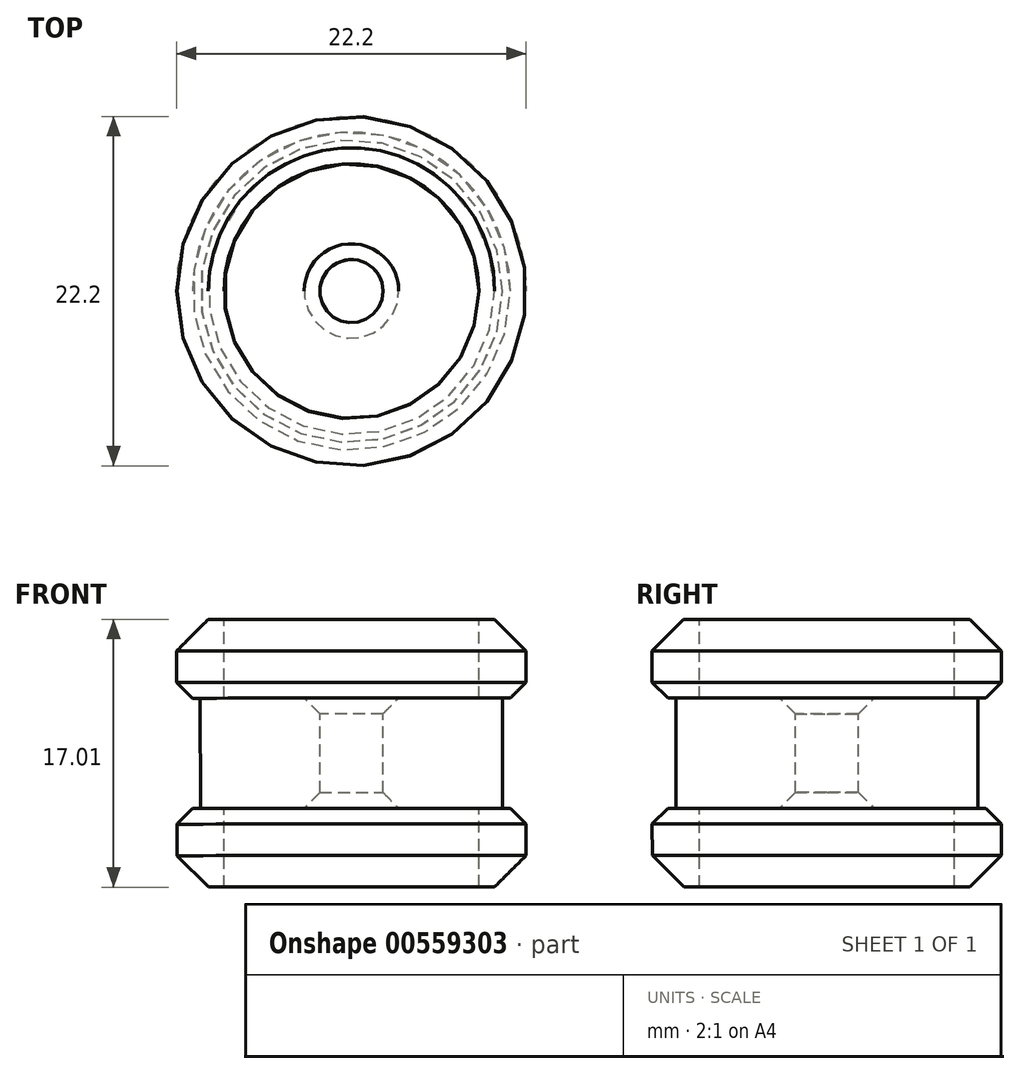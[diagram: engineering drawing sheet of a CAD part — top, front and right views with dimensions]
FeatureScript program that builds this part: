
annotation { "Feature Type Name" : "Feature", "Feature Type Description" : "" }
export const myFeature = defineFeature(function(context is Context, id is Id, definition is map)
    precondition{}
    {
        {
            var Q0;
            Q0=qCreatedBy(makeId("Front.planeOp"),FACE);
            var sketch = newSketch(context, id + "F0", { "sketchPlane" : qUnion([Q0])});
            skLineSegment(sketch, "E0", {"start": v(-8.11, 2.26) * mm, "end": v(8.09, 2.26) * mm, "construction": true});
            skLineSegment(sketch, "E1", {"start": v(8.09, 2.26) * mm, "end": v(11.09, 2.26) * mm});
            skLineSegment(sketch, "E2", {"start": v(11.09, 2.26) * mm, "end": v(11.09, -2.74) * mm});
            skLineSegment(sketch, "E3", {"start": v(11.09, -2.74) * mm, "end": v(8.09, -2.74) * mm});
            skLineSegment(sketch, "E4", {"start": v(8.09, -2.74) * mm, "end": v(8.09, 2.26) * mm});
            skLineSegment(sketch, "E5", {"start": v(9.59, -2.74) * mm, "end": v(9.59, -9.74) * mm});
            skLineSegment(sketch, "E6", {"start": v(8.09, -9.74) * mm, "end": v(11.09, -9.74) * mm});
            skLineSegment(sketch, "E7", {"start": v(11.09, -9.74) * mm, "end": v(11.09, -14.74) * mm});
            skLineSegment(sketch, "E8", {"start": v(11.09, -14.74) * mm, "end": v(8.09, -14.74) * mm});
            skLineSegment(sketch, "E9", {"start": v(8.09, -14.74) * mm, "end": v(8.09, -9.74) * mm});
            skLineSegment(sketch, "E10", {"start": v(-0.01, 2.26) * mm, "end": v(0, -14.74) * mm});
            skLineSegment(sketch, "E11", {"start": v(2, -2.74) * mm, "end": v(0, -2.74) * mm});
            skLineSegment(sketch, "E12", {"start": v(2, -2.74) * mm, "end": v(8.09, -2.74) * mm});
            skLineSegment(sketch, "E13", {"start": v(2, -2.74) * mm, "end": v(2, -9.74) * mm});
            skLineSegment(sketch, "E14", {"start": v(2, -9.74) * mm, "end": v(8.09, -9.74) * mm});
            skSolve(sketch);
        }
        {
            var Q0;
            Q0 = qSketchRegion(id + "F0", true);
            var Q1;
            Q1=sQuery(id+"F0.wireOp",EDGE,"E10");
            revolve(context, id + "F1", {"surfaceOperationType" : NewSurfaceOperationType.NEW, "entities" : qUnion([Q0]), "axis" : qUnion([Q1]), "revolveType" : RevolveType.FULL});
        }
        {
            var Q0;
            Q0=makeQuery(id+"F1.opRevolve","SWEPT_EDGE",EDGE,{"disambiguationData":[OSD([sQuery(id+"F0.wireOp",EDGE,"E7"),sQuery(id+"F0.wireOp",EDGE,"E8")])]});
            var Q1;
            Q1=makeQuery(id+"F1.opRevolve","SWEPT_EDGE",EDGE,{"disambiguationData":[OSD([sQuery(id+"F0.wireOp",EDGE,"E1"),sQuery(id+"F0.wireOp",EDGE,"E2")])]});
            chamfer(context, id + "F2", {"entities" : qUnion([Q0, Q1]), "width" : 2 * mm, "tangentPropagation" : true});
        }
        {
            var Q0;
            Q0=makeQuery(id+"F1.opRevolve","SWEPT_EDGE",EDGE,{"disambiguationData":[OSD([sQuery(id+"F0.wireOp",EDGE,"E2"),sQuery(id+"F0.wireOp",EDGE,"E3")])]});
            var Q1;
            Q1=makeQuery(id+"F1.opRevolve","SWEPT_EDGE",EDGE,{"disambiguationData":[OSD([sQuery(id+"F0.wireOp",EDGE,"E6"),sQuery(id+"F0.wireOp",EDGE,"E7")])]});
            var Q2;
            Q2=makeQuery(id+"F1.opRevolve","SWEPT_EDGE",EDGE,{"disambiguationData":[OSD([sQuery(id+"F0.wireOp",EDGE,"E12"),sQuery(id+"F0.wireOp",EDGE,"E13")])]});
            var Q3;
            Q3=makeQuery(id+"F1.opRevolve","SWEPT_EDGE",EDGE,{"disambiguationData":[OSD([sQuery(id+"F0.wireOp",EDGE,"E13"),sQuery(id+"F0.wireOp",EDGE,"E14")])]});
            chamfer(context, id + "F3", {"entities" : qUnion([Q0, Q1, Q2, Q3]), "width" : 1 * mm, "tangentPropagation" : true});
        }
    });
